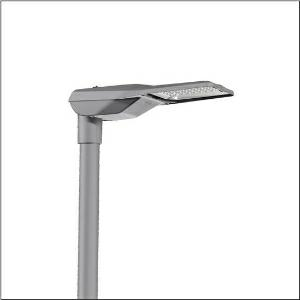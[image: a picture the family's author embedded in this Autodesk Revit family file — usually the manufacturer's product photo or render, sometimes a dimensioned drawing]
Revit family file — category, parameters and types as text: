
# Revit family: streetlight_sl_21_mini___stw1_0a_5xe2e33s08jb_3b81
name_source: partatom
category: Lighting Fixtures
units: mm (PartAtom-declared; Revit-internal decimal feet)

## family parameters
Cut with Voids When Loaded = No
Host = Face
Light Source = No
Part Type = Normal
Room Calculation Point = No
Round Connector Dimension = Use Diameter
Shared = No

## types (1)
- --- (1 x LED, 12940 lm, 88.6 W, 3000K)
    Apparent Load = 89 VA
    CIE Flux Codes = 39 75 98 100 100
    Color Rendering = 70
    Color Temperature = 3000K
    Default Elevation = 1800 mm
    Description = Streetlight SL 21 mini, mast luminaire, primary light control with lens, of PMMA, primary optical cover: cover, of toughened safety glass, transparent, light distribution: STW1.0a, light emission: direct distribution, primary light characteristic: asymmetric, installation type: side-entry, post-top, LED, High Power LED, rated luminous flux: 12.940lm, luminous efficacy: 146lm/W, light colour: 730, colour temperature: 3000K, control gear: D4i, control: overheat protection, constant luminous flux control, time-dependent luminous flux control, flexible luminous flux parameterisation, pre-setting: logarithmic dimming characteristic, mains connection: 220..240V, AC, 50/60Hz, start of lifetime: 89W, end of service life: 92W, reduction: 41W, luminaire housing, of diecast aluminium, powder-coated, SITECO metallic grey (DB 702S), corrosivity category C5 high according to DIN EN ISO 12944, please order mast flange separately, inclination adjustable: 0°, 5°, 10°, 15°, sealing non-destructively replaceable, multi-level sealing system, length: 628mm, width: 235mm, height: 110mm, mast flange for spigot size: 42mm (side-entry): 5XC10008XM4, 60/48mm (side-entry/post-top): 5XC10108XM2, 76/60mm (side-entry/post-top): 5XC10108XM1, mounting height: 4..8m, Smart Interface above, protection rating (complete): IP66, insulation class (complete): insulation class II (safety insulation), certification: CE, ENEC, ENEC+, VDE, impact resistance: IK10, permissible operating ambient temperature for outdoor applications: -40..+50°C, standard-compliant lighting for roads and squares, packaging unit: 1 piece

Light Distribution: STW1.0a
    Height = 110 mm
    Lamp = 1 x LED
    Lamp Light Flux = 12940 lm
    Lamp Power = 88.6 W
    Lamp count = 1
    Length = 625 mm
    Luminous efficacy = 146 lm/W
    Manufacturer = Siteco
    ModVariant = No
    Model = 5XE2E33S08JB
    Number of Poles = 1
    OnlyDefault = Yes
    Power Factor = 1
    Product Name = Streetlight SL 21 mini | STW1.0a
    Product group = mast luminaire | pylon top
    ProductGroupID = 6100
    Protection Class = Protection class II
    Protection Degree = IP 66
    RLX_Detail_Level = 1
    RLX_Emergency_Light_Flux = 0 lm
    RLX_Emergency_Type = 0
    RLX_Emergency_Type_DB = No
    RlxData = <blob elided: 26277 chars, md5=f56f02f4>
    Socket = socket
    Standby Power = 0 W
    System Light Flux = 12940 lm
    System Power = 89 W
    Type Comments = factory setting: luminous flux: 100 % | dim-lin: 254 | 915 mA
    Type Image = l_1003515.jpg
    URL = http://relux.com
    VarID = @adj_031121
    Voltage = 0 V
    Weight = 0.00 kg
    Width = 234 mm

## geometry (parser evidence)
native form markers: Blend x4, Sweep x10
no freeform markers — native parametric forms only
